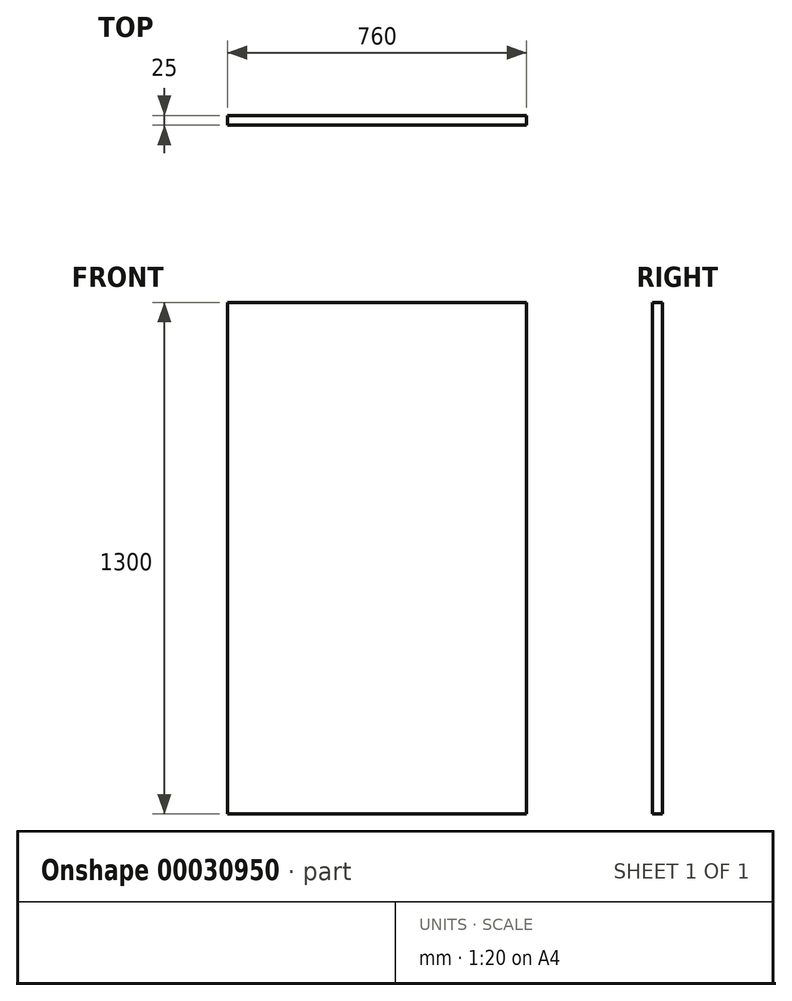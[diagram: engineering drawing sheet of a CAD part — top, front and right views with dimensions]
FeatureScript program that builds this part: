
annotation { "Feature Type Name" : "Feature", "Feature Type Description" : "" }
export const myFeature = defineFeature(function(context is Context, id is Id, definition is map)
    precondition{}
    {
        {
            var Q0;
            Q0=qCreatedBy(makeId("Front.planeOp"),FACE);
            var sketch = newSketch(context, id + "F0", { "sketchPlane" : qUnion([Q0])});
            skLineSegment(sketch, "E0.rect.bottom", {"start": v(-380, 650) * mm, "end": v(380, 650) * mm});
            skLineSegment(sketch, "E0.rect.top", {"start": v(-380, -650) * mm, "end": v(380, -650) * mm});
            skLineSegment(sketch, "E0.rect.left", {"start": v(-380, 650) * mm, "end": v(-380, -650) * mm});
            skLineSegment(sketch, "E0.rect.right", {"start": v(380, 650) * mm, "end": v(380, -650) * mm});
            skPoint(sketch, "E0.rect.middle", {"position": v(0, 0) * mm});
            skSolve(sketch);
        }
        {
            var Q0;
            Q0=makeQuery(id+"F0.imprint","IMPRINT",FACE,{"disambiguationData":[TD([[makeQuery(id+"F0.imprint","IMPRINT",EDGE,{"derivedFrom":sQuery(id+"F0.wireOp",EDGE,"E0.rect.bottom")}),-1.0]])]});
            extrude(context, id + "F1", {"entities" : qUnion([Q0]), "depth" : 25 * mm});
        }
    });
